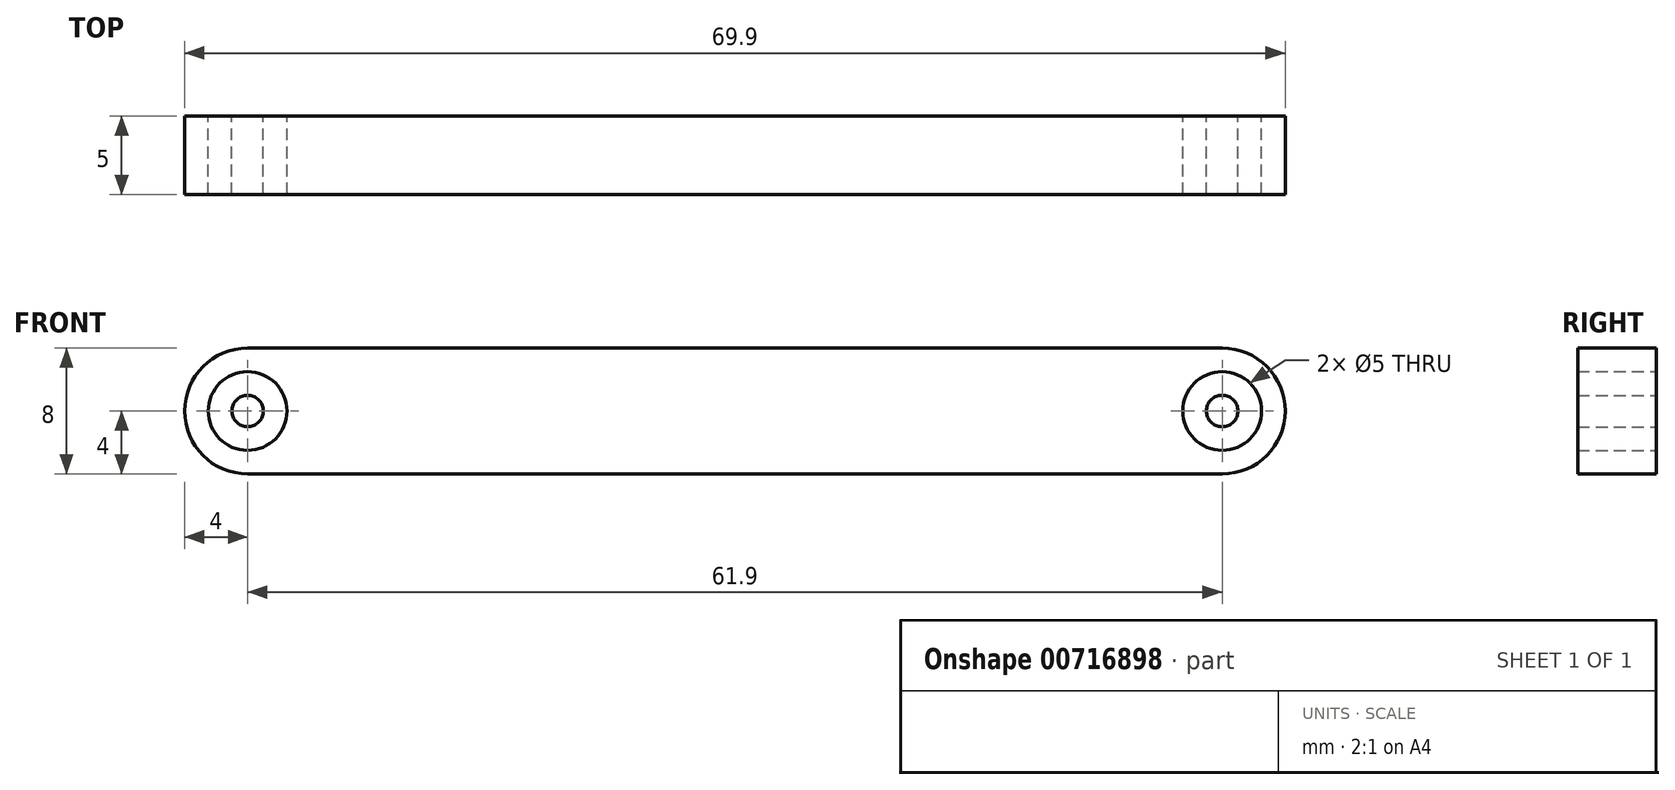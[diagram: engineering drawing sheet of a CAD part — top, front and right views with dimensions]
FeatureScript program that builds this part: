
annotation { "Feature Type Name" : "Feature", "Feature Type Description" : "" }
export const myFeature = defineFeature(function(context is Context, id is Id, definition is map)
    precondition{}
    {
        {
            var Q0;
            Q0=qCreatedBy(makeId("Front.planeOp"),FACE);
            var sketch = newSketch(context, id + "F0", { "sketchPlane" : qUnion([Q0])});
            skArc(sketch, "E0", {"start": v(0, -4) * mm, "mid": v(4, 0) * mm, "end": v(0, 4) * mm});
            skArc(sketch, "E1", {"start": v(-61.9, 4) * mm, "mid": v(-65.9, 0) * mm, "end": v(-61.9, -4) * mm});
            skLineSegment(sketch, "E2", {"start": v(0, 4) * mm, "end": v(-61.9, 4) * mm});
            skLineSegment(sketch, "E3", {"start": v(0, -4) * mm, "end": v(-61.9, -4) * mm});
            skCircle(sketch, "E4", {"center": v(0, 0) * mm, "radius": 2.5 * mm});
            skCircle(sketch, "E5", {"center": v(-61.9, 0) * mm, "radius": 2.5 * mm});
            skCircle(sketch, "E6", {"center": v(0, 0) * mm, "radius": 1 * mm});
            skCircle(sketch, "E7", {"center": v(-61.9, 0) * mm, "radius": 1 * mm});
            skSolve(sketch);
        }
        {
            var Q0;
            Q0 = qSketchRegion(id + "F0", true);
            var Q1;
            Q1=makeQuery(id+"F0.imprint","IMPRINT",FACE,{"disambiguationData":[TD([[makeQuery(id+"F0.imprint","IMPRINT",EDGE,{"derivedFrom":sQuery(id+"F0.wireOp",EDGE,"E7")}),1.0]])]});
            var Q2;
            Q2=makeQuery(id+"F0.imprint","IMPRINT",FACE,{"disambiguationData":[TD([[makeQuery(id+"F0.imprint","IMPRINT",EDGE,{"derivedFrom":sQuery(id+"F0.wireOp",EDGE,"E6")}),1.0]])]});
            extrude(context, id + "F1", {"entities" : qUnion([Q0, Q1, Q2]), "depth" : 5 * mm, "offsetDistance" : 25.4 * mm});
        }
    });
